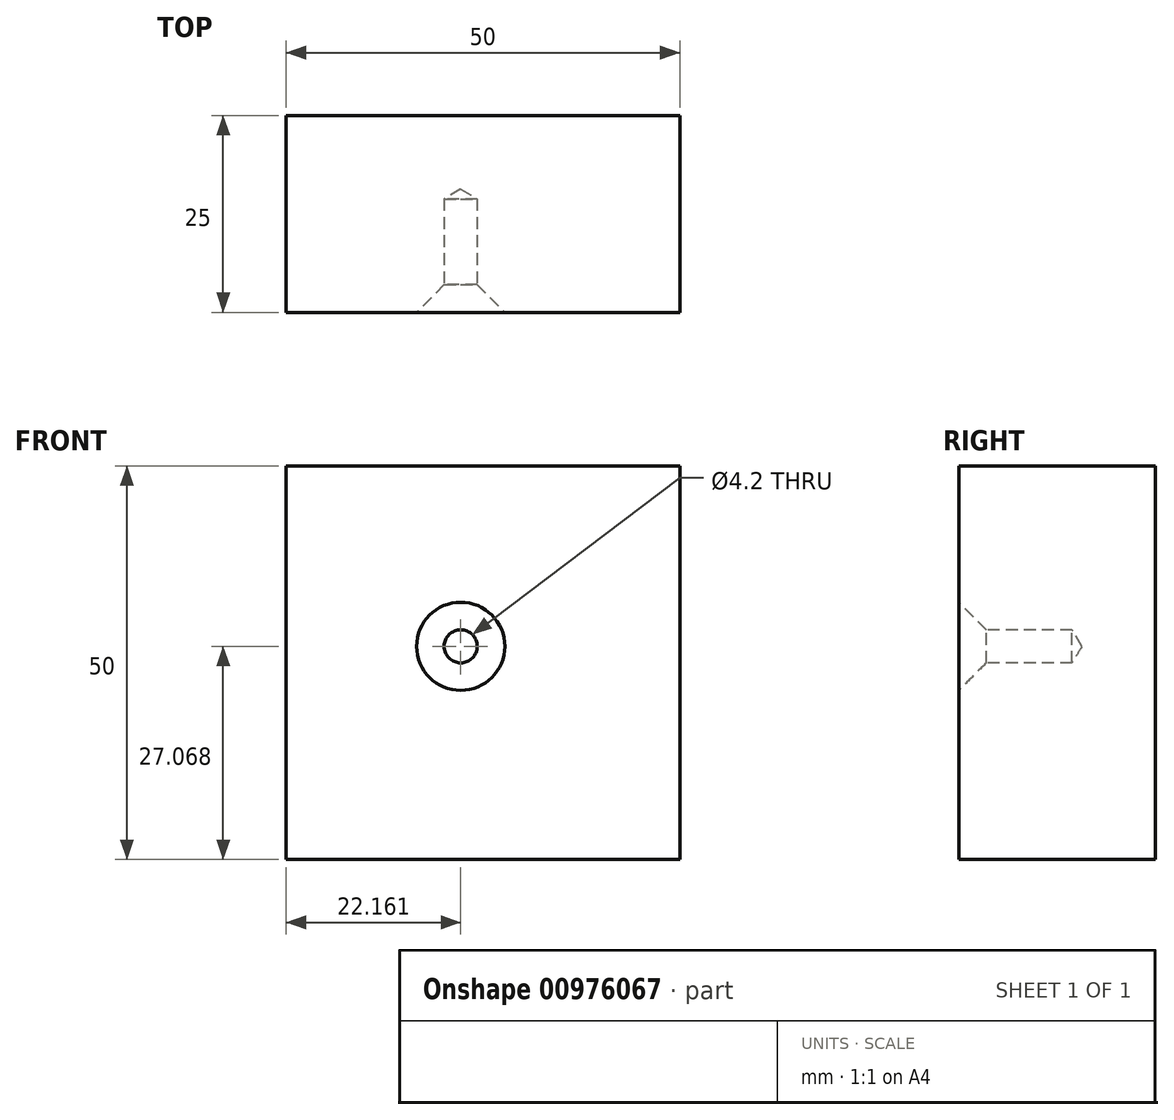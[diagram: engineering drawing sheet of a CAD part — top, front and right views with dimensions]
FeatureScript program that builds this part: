
annotation { "Feature Type Name" : "Feature", "Feature Type Description" : "" }
export const myFeature = defineFeature(function(context is Context, id is Id, definition is map)
    precondition{}
    {
        {
            var Q0;
            Q0=qCreatedBy(makeId("Front.planeOp"),FACE);
            var sketch = newSketch(context, id + "F0", { "sketchPlane" : qUnion([Q0])});
            skLineSegment(sketch, "E0.bottom", {"start": v(-109.75, 55.55) * mm, "end": v(-59.75, 55.55) * mm});
            skLineSegment(sketch, "E0.top", {"start": v(-109.75, 5.55) * mm, "end": v(-59.75, 5.55) * mm});
            skLineSegment(sketch, "E0.left", {"start": v(-109.75, 55.55) * mm, "end": v(-109.75, 5.55) * mm});
            skLineSegment(sketch, "E0.right", {"start": v(-59.75, 55.55) * mm, "end": v(-59.75, 5.55) * mm});
            skSolve(sketch);
        }
        {
            var Q0;
            Q0 = qSketchRegion(id + "F0", true);
            extrude(context, id + "F1", {"entities" : qUnion([Q0]), "depth" : 25 * mm, "offsetDistance" : 25 * mm});
        }
        {
            var Q0;
            Q0=makeQuery(id+"F1.opExtrude","CAP_FACE",FACE,{"disambiguationData":[OSD([sQuery(id+"F0.wireOp",EDGE,"E0.bottom"),sQuery(id+"F0.wireOp",EDGE,"E0.top"),sQuery(id+"F0.wireOp",EDGE,"E0.left"),sQuery(id+"F0.wireOp",EDGE,"E0.right")])],"isStart":false});
            var sketch = newSketch(context, id + "F2", { "sketchPlane" : qUnion([Q0])});
            skPoint(sketch, "E1", {"position": v(-87.59, 32.62) * mm});
            skSolve(sketch);
        }
        {
            var Q0;
            Q0=sQuery(id+"F2.wireOp",VERTEX,"E1");
            var Q1;
            Q1=makeQuery(id+"F1.opExtrude","SWEPT_BODY",BODY,{"disambiguationData":[OSD([sQuery(id+"F0.wireOp",EDGE,"E0.bottom"),sQuery(id+"F0.wireOp",EDGE,"E0.top"),sQuery(id+"F0.wireOp",EDGE,"E0.left"),sQuery(id+"F0.wireOp",EDGE,"E0.right")])]});
            hole(context, id + "F3", {"style" : HoleStyle.C_SINK, "endStyle" : HoleEndStyle.BLIND, "holeDiameter" : 4.2 * mm, "cSinkDiameter" : 11.2 * mm, "cSinkAngle" : 90 * degree, "majorDiameter" : 5 * mm, "holeDepth" : 14.4 * mm, "isTappedThrough" : true, "tappedDepth" : 12 * mm, "tapClearance" : 3, "startFromSketch" : true, "locations" : qUnion([Q0]), "scope" : qUnion([Q1])});
        }
    });
